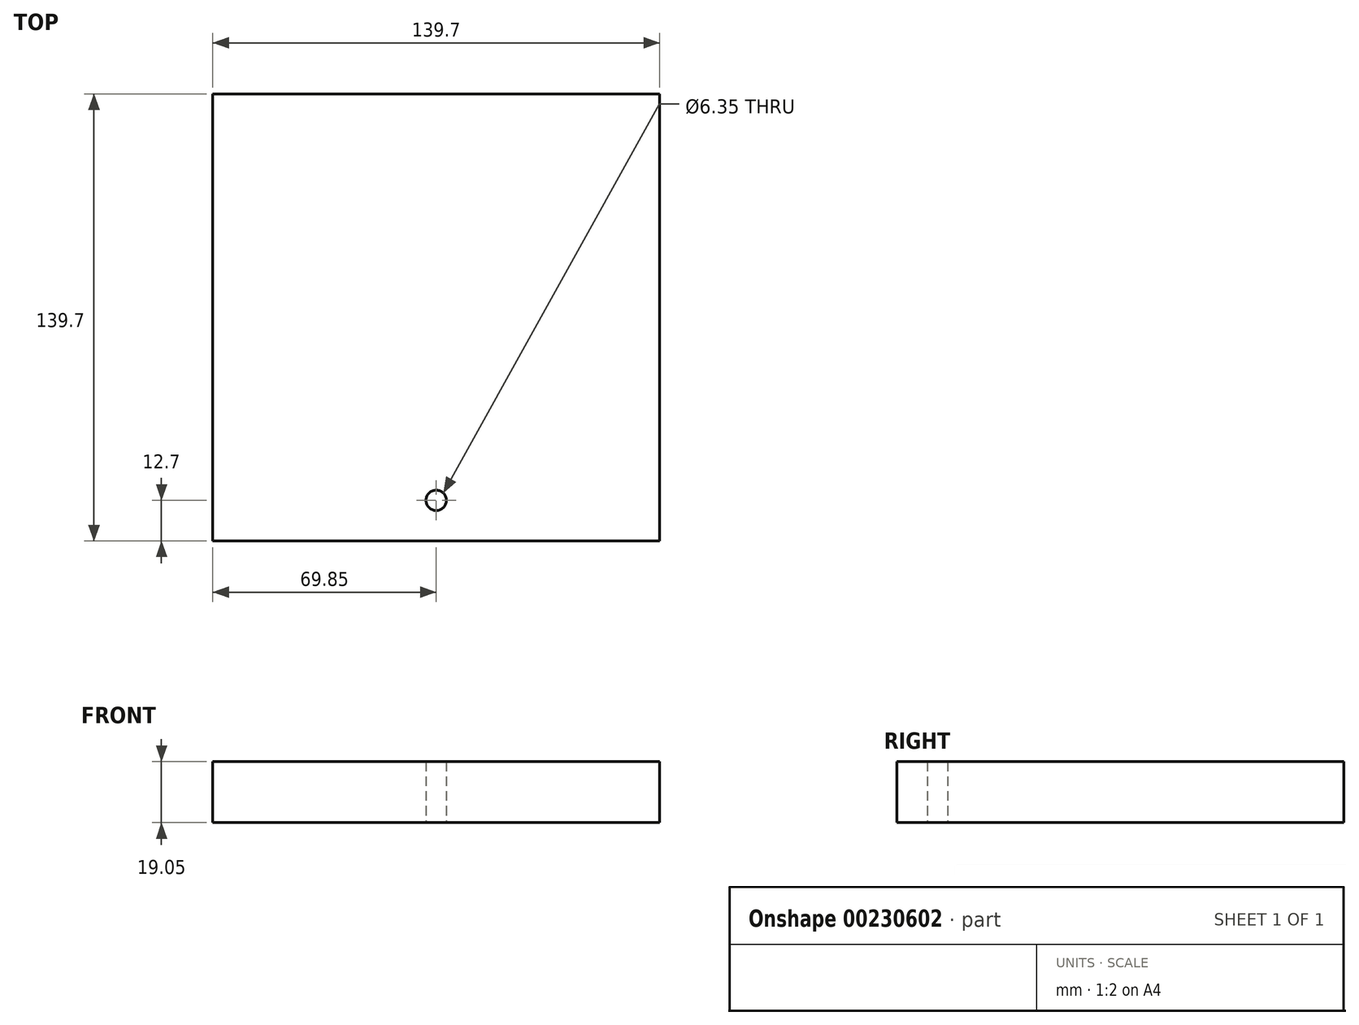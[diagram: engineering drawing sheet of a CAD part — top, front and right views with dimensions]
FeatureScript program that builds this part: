
annotation { "Feature Type Name" : "Feature", "Feature Type Description" : "" }
export const myFeature = defineFeature(function(context is Context, id is Id, definition is map)
    precondition{}
    {
        {
            var Q0;
            Q0=qCreatedBy(makeId("Top.planeOp"),FACE);
            var sketch = newSketch(context, id + "F0", { "sketchPlane" : qUnion([Q0])});
            skLineSegment(sketch, "E0.bottom", {"start": v(-69.85, 69.85) * mm, "end": v(69.85, 69.85) * mm});
            skLineSegment(sketch, "E0.top", {"start": v(-69.85, -69.85) * mm, "end": v(69.85, -69.85) * mm});
            skLineSegment(sketch, "E0.left", {"start": v(-69.85, 69.85) * mm, "end": v(-69.85, -69.85) * mm});
            skLineSegment(sketch, "E0.right", {"start": v(69.85, 69.85) * mm, "end": v(69.85, -69.85) * mm});
            skPoint(sketch, "E0.middle", {"position": v(0, 0) * mm});
            skLineSegment(sketch, "E1", {"start": v(0, -69.85) * mm, "end": v(0, -57.15) * mm});
            skPoint(sketch, "E1.endSnap0", {"position": v(0, -69.85) * mm});
            skCircle(sketch, "E2", {"center": v(0, -57.15) * mm, "radius": 3.18 * mm});
            skSolve(sketch);
        }
        {
            var Q0;
            Q0=makeQuery(id+"F0.imprint","IMPRINT",FACE,{"disambiguationData":[TD([[makeQuery(id+"F0.imprint","IMPRINT",EDGE,{"derivedFrom":sQuery(id+"F0.wireOp",EDGE,"E0.bottom")}),-1.0]])]});
            extrude(context, id + "F1", {"entities" : qUnion([Q0]), "depth" : 19.05 * mm});
        }
        {
            var Q0;
            Q0 = qSketchRegion(id + "F0", true);
            extrude(context, id + "F2", {"entities" : qUnion([Q0]), "operationType" : NewBodyOperationType.ADD, "depth" : 19.05 * mm});
        }
    });
